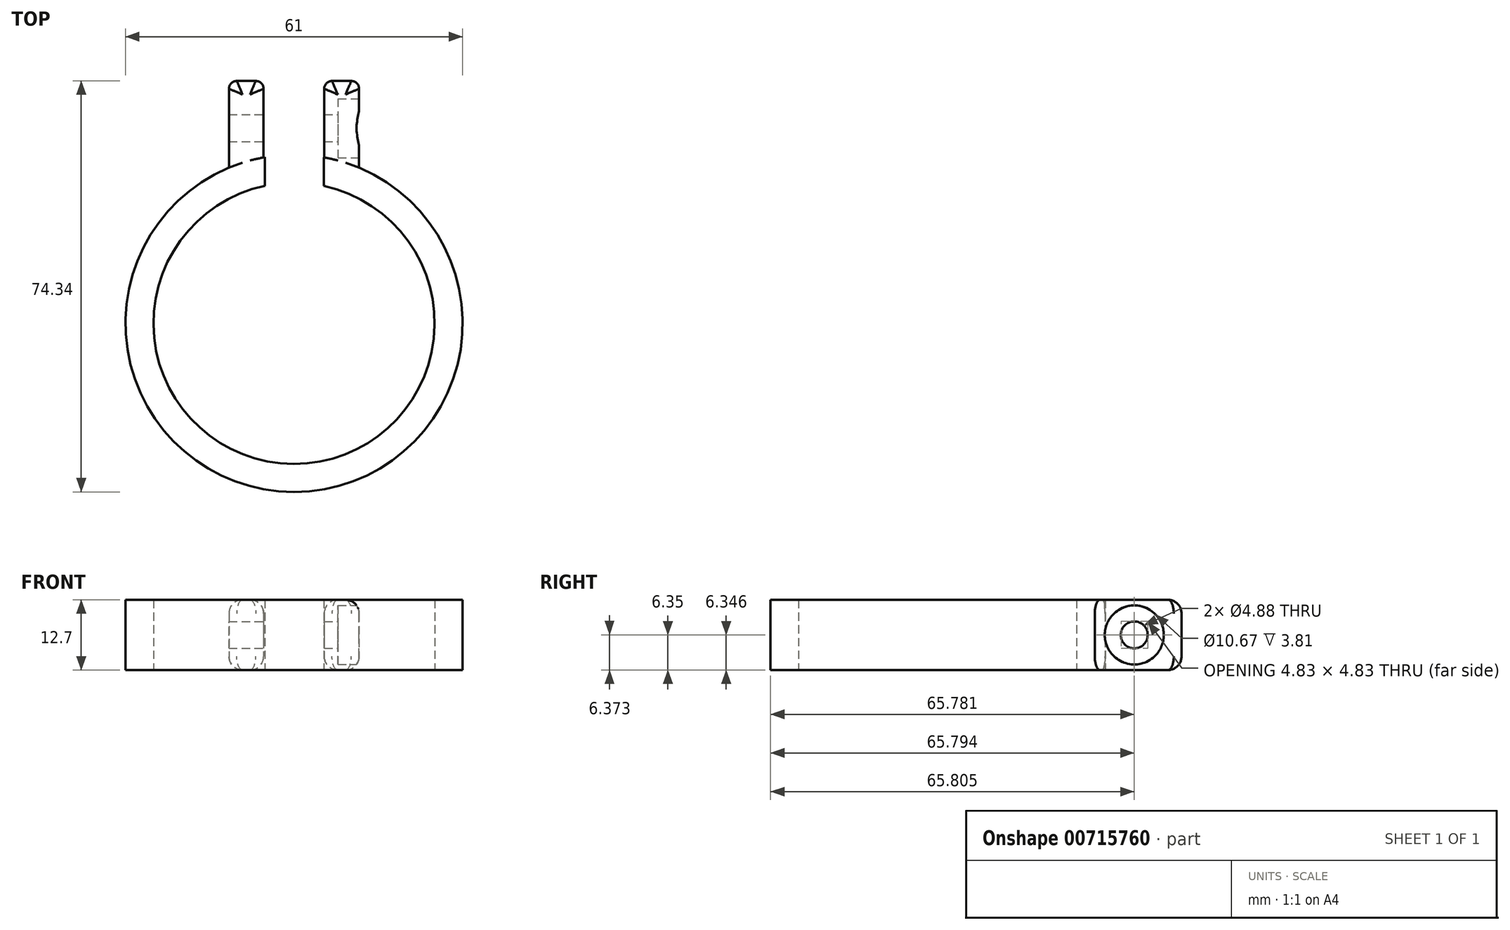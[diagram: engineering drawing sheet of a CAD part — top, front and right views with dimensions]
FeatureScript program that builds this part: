
annotation { "Feature Type Name" : "Feature", "Feature Type Description" : "" }
export const myFeature = defineFeature(function(context is Context, id is Id, definition is map)
    precondition{}
    {
        {
            var Q0;
            Q0=qCreatedBy(makeId("Top.planeOp"),FACE);
            var sketch = newSketch(context, id + "F0", { "sketchPlane" : qUnion([Q0])});
            skCircle(sketch, "E0", {"center": v(0, 0) * mm, "radius": 25.43 * mm});
            skCircle(sketch, "E1", {"center": v(0, 0) * mm, "radius": 30.5 * mm});
            skLineSegment(sketch, "E2", {"start": v(-5.5, 24.82) * mm, "end": v(-5.5, 43.84) * mm});
            skLineSegment(sketch, "E3", {"start": v(5.46, 24.83) * mm, "end": v(5.46, 43.84) * mm});
            skLineSegment(sketch, "E4", {"start": v(5.46, 43.84) * mm, "end": v(11.77, 43.84) * mm});
            skLineSegment(sketch, "E5", {"start": v(11.77, 43.84) * mm, "end": v(11.77, 22.54) * mm});
            skLineSegment(sketch, "E6", {"start": v(-5.5, 43.84) * mm, "end": v(-11.77, 43.84) * mm});
            skLineSegment(sketch, "E7", {"start": v(-11.77, 43.84) * mm, "end": v(-11.77, 22.54) * mm});
            skSolve(sketch);
        }
        {
            var Q0;
            Q0 = qSketchRegion(id + "F0", true);
            extrude(context, id + "F1", {"entities" : qUnion([Q0]), "depth" : 12.7 * mm, "offsetDistance" : 25.4 * mm});
        }
        {
            var Q0;
            Q0=makeQuery(id+"F1.opExtrude","SWEPT_EDGE",EDGE,{"disambiguationData":[OSD([sQuery(id+"F0.wireOp",EDGE,"E2"),sQuery(id+"F0.wireOp",EDGE,"E6")])]});
            var Q1;
            Q1=makeQuery(id+"F1.opExtrude","SWEPT_EDGE",EDGE,{"disambiguationData":[OSD([sQuery(id+"F0.wireOp",EDGE,"E6"),sQuery(id+"F0.wireOp",EDGE,"E7")])]});
            var Q2;
            Q2=makeQuery(id+"F1.opExtrude","SWEPT_EDGE",EDGE,{"disambiguationData":[OSD([sQuery(id+"F0.wireOp",EDGE,"E3"),sQuery(id+"F0.wireOp",EDGE,"E4")])]});
            var Q3;
            Q3=makeQuery(id+"F1.opExtrude","SWEPT_EDGE",EDGE,{"disambiguationData":[OSD([sQuery(id+"F0.wireOp",EDGE,"E4"),sQuery(id+"F0.wireOp",EDGE,"E5")])]});
            fillet(context, id + "F2", {"entities" : qUnion([Q0, Q1, Q2, Q3]), "radius" : 1.41 * mm, "tangentPropagation" : true, "allowEdgeOverflow" : false});
        }
        {
            var Q0;
            Q0=makeQuery(id+"F1.opExtrude","CAP_EDGE",EDGE,{"disambiguationData":[OSD([sQuery(id+"F0.wireOp",EDGE,"E6")])],"isStart":false});
            var Q1;
            Q1=makeQuery(id+"F1.opExtrude","CAP_EDGE",EDGE,{"disambiguationData":[OSD([sQuery(id+"F0.wireOp",EDGE,"E6")])],"isStart":true});
            var Q2;
            Q2=makeQuery(id+"F1.opExtrude","CAP_EDGE",EDGE,{"disambiguationData":[OSD([sQuery(id+"F0.wireOp",EDGE,"E4")])],"isStart":false});
            var Q3;
            Q3=makeQuery(id+"F1.opExtrude","CAP_EDGE",EDGE,{"disambiguationData":[OSD([sQuery(id+"F0.wireOp",EDGE,"E4")])],"isStart":true});
            fillet(context, id + "F3", {"entities" : qUnion([Q0, Q1, Q2, Q3]), "radius" : 2.45 * mm, "tangentPropagation" : true, "allowEdgeOverflow" : false});
        }
        {
            var Q0;
            Q0=qCreatedBy(makeId("Top.planeOp"),FACE);
            var sketch = newSketch(context, id + "F4", { "sketchPlane" : qUnion([Q0])});
            skLineSegment(sketch, "E8.bottom", {"start": v(-5.27, 30.29) * mm, "end": v(5.4, 30.29) * mm});
            skLineSegment(sketch, "E8.top", {"start": v(-5.27, 18.47) * mm, "end": v(5.4, 18.47) * mm});
            skLineSegment(sketch, "E8.left", {"start": v(-5.27, 30.29) * mm, "end": v(-5.27, 18.47) * mm});
            skLineSegment(sketch, "E8.right", {"start": v(5.4, 30.29) * mm, "end": v(5.4, 18.47) * mm});
            skLineSegment(sketch, "E9.bottom", {"start": v(5.4, 30.29) * mm, "end": v(5.4, 30.29) * mm});
            skLineSegment(sketch, "E9.top", {"start": v(5.4, 33.5) * mm, "end": v(5.4, 33.5) * mm});
            skLineSegment(sketch, "E9.left", {"start": v(5.4, 30.29) * mm, "end": v(5.4, 33.5) * mm});
            skLineSegment(sketch, "E9.right", {"start": v(5.4, 30.29) * mm, "end": v(5.4, 33.5) * mm});
            skLineSegment(sketch, "E10.bottom", {"start": v(-5.27, 30.29) * mm, "end": v(-5.27, 30.29) * mm});
            skLineSegment(sketch, "E10.top", {"start": v(-5.27, 33.5) * mm, "end": v(-5.27, 33.5) * mm});
            skLineSegment(sketch, "E10.left", {"start": v(-5.27, 30.29) * mm, "end": v(-5.27, 33.5) * mm});
            skLineSegment(sketch, "E10.right", {"start": v(-5.27, 30.29) * mm, "end": v(-5.27, 33.5) * mm});
            skLineSegment(sketch, "E11.bottom", {"start": v(5.4, 33.5) * mm, "end": v(-5.27, 33.5) * mm});
            skLineSegment(sketch, "E11.top", {"start": v(5.4, 34.52) * mm, "end": v(-5.27, 34.52) * mm});
            skLineSegment(sketch, "E11.left", {"start": v(5.4, 33.5) * mm, "end": v(5.4, 34.52) * mm});
            skLineSegment(sketch, "E11.right", {"start": v(-5.27, 33.5) * mm, "end": v(-5.27, 34.52) * mm});
            skSolve(sketch);
        }
        {
            var Q0;
            Q0 = qSketchRegion(id + "F4", true);
            extrude(context, id + "F5", {"entities" : qUnion([Q0]), "operationType" : NewBodyOperationType.REMOVE, "depth" : 43.43 * mm, "offsetDistance" : 25.4 * mm});
        }
        {
            var Q0;
            Q0=makeQuery(id+"F1.opExtrude","SWEPT_FACE",FACE,{"disambiguationData":[OSD([sQuery(id+"F0.wireOp",EDGE,"E5")])]});
            var sketch = newSketch(context, id + "F6", { "sketchPlane" : qUnion([Q0])});
            skCircle(sketch, "E12", {"center": v(35.28, 6.35) * mm, "radius": 2.44 * mm});
            skPoint(sketch, "E12.centerSnap0", {"position": v(42.43, 6.35) * mm});
            skPoint(sketch, "E12.centerSnap1", {"position": v(35.28, 10.25) * mm});
            skSolve(sketch);
        }
        {
            var Q0;
            Q0 = qSketchRegion(id + "F6", true);
            extrude(context, id + "F7", {"entities" : qUnion([Q0]), "operationType" : NewBodyOperationType.REMOVE, "oppositeDirection" : true, "depth" : 25.4 * mm, "offsetDistance" : 25.4 * mm});
        }
        {
            var Q0;
            Q0=makeQuery(id+"F6.imprint","IMPRINT",FACE,{"disambiguationData":[TD([[makeQuery(id+"F6.imprint","IMPRINT",EDGE,{"derivedFrom":sQuery(id+"F6.wireOp",EDGE,"E12")}),-1.0]])]});
            var sketch = newSketch(context, id + "F8", { "sketchPlane" : qUnion([Q0])});
            skCircle(sketch, "E13", {"center": v(35.3, 6.35) * mm, "radius": 5.33 * mm});
            skSolve(sketch);
        }
        {
            var Q0;
            Q0 = qSketchRegion(id + "F8", true);
            extrude(context, id + "F9", {"entities" : qUnion([Q0]), "operationType" : NewBodyOperationType.REMOVE, "oppositeDirection" : true, "depth" : 3.8 * mm, "offsetDistance" : 25.4 * mm});
        }
    });
